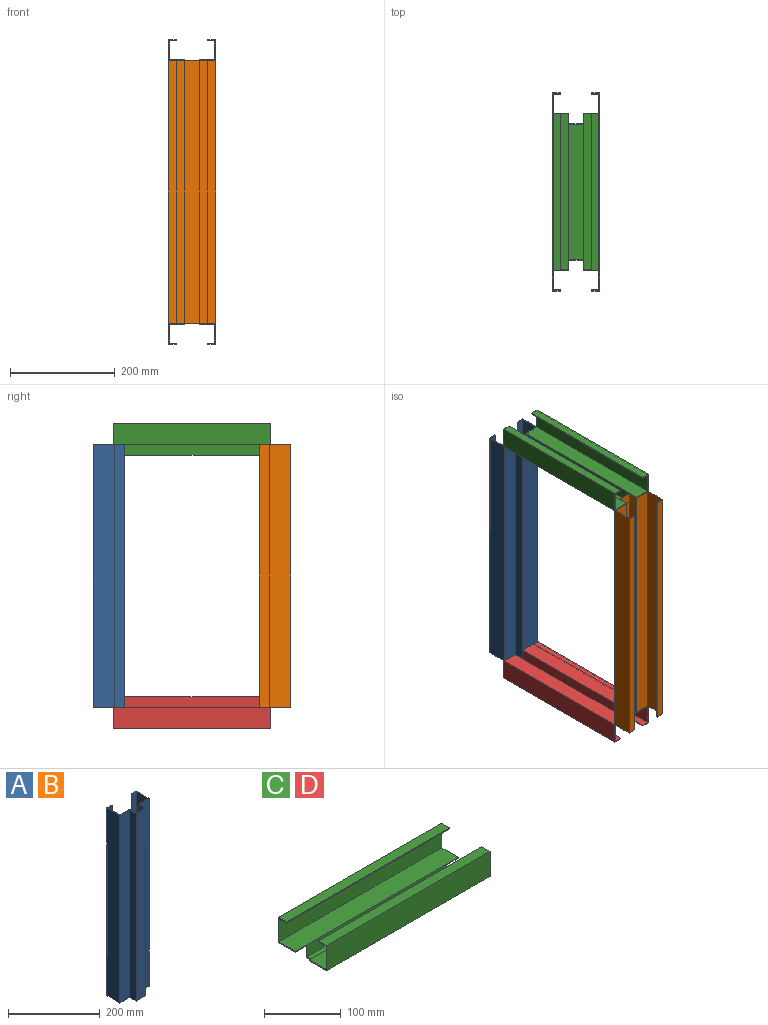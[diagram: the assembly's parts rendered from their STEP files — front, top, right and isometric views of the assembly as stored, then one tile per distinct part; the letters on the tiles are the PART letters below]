
ASSEMBLY  parts=4 mates=12
PART A: 22 faces, bbox 90x60x500 mm
  f0: plane 500x20mm, normal (-1,0,0), area 10000mm2, adj f1,f19,f20,f21
  f1: plane 500x30mm, normal (0,-1,0), area 15000mm2, adj f0,f2,f20,f21
  f2: plane 500x20mm, normal (1,0,0), area 10000mm2, adj f1,f3,f20,f21
  f3: plane 500x30mm, normal (0,-1,0), area 15000mm2, adj f2,f4,f20,f21
  f4: plane 500x40mm, normal (1,0,0), area 20000mm2, adj f3,f5,f20,f21
  f5: plane 500x15mm, normal (0,1,0), area 7500mm2, adj f4,f6,f20,f21
  f6: plane 500x1.6mm, normal (-1,0,0), area 800mm2, adj f5,f7,f20,f21
  f7: plane 500x13.4mm, normal (0,-1,0), area 6700mm2, adj f6,f8,f20,f21
  f8: plane 500x36.8mm, normal (-1,0,0), area 18400mm2, adj f7,f9,f20,f21
  f9: plane 500x30mm, normal (0,1,0), area 15000mm2, adj f8,f10,f20,f21
  f10: plane 500x20mm, normal (-1,0,0), area 10000mm2, adj f9,f11,f20,f21
  f11: plane 500x26.8mm, normal (0,1,0), area 13400mm2, adj f10,f12,f20,f21
  f12: plane 500x20mm, normal (1,0,0), area 10000mm2, adj f11,f13,f20,f21
  f13: plane 500x30mm, normal (0,1,0), area 15000mm2, adj f12,f14,f20,f21
  f14: plane 500x36.8mm, normal (1,0,0), area 18400mm2, adj f13,f15,f20,f21
  f15: plane 500x13.4mm, normal (0,-1,0), area 6700mm2, adj f14,f16,f20,f21
  f16: plane 500x1.6mm, normal (1,0,0), area 800mm2, adj f15,f17,f20,f21
  f17: plane 500x15mm, normal (0,1,0), area 7500mm2, adj f16,f18,f20,f21
  f18: plane 500x40mm, normal (-1,0,0), area 20000mm2, adj f17,f19,f20,f21
  f19: plane 500x30mm, normal (0,-1,0), area 15000mm2, adj f0,f18,f20,f21
  f20: plane 90x60mm, normal (0,0,1), area 373.8mm2, adj f0,f1,f2,f3,f4,f5,f6,f7
  f21: plane 90x60mm, normal (0,0,-1), area 373.8mm2, adj f0,f1,f2,f3,f4,f5,f6,f7
PART B: same geometry as A
PART C: 26 faces, bbox 300x90x60 mm
  f0: plane 256.8x20mm, normal (0,-1,0), area 5136mm2, adj f1,f23,f24,f25
  f1: plane 256.8x30mm, normal (0,0,-1), area 7704mm2, adj f0,f2,f24,f25
  f2: plane 256.8x20mm, normal (0,1,0), area 5136mm2, adj f1,f8,f24,f25
  f3: plane 256.8x26.8mm, normal (0,0,1), area 6882.2mm2, adj f15,f16,f24,f25
  f4: plane 40x31.6mm, normal (1,0,0), area 133.4mm2, adj f16,f17,f18,f19,f20,f21,f22,f23
  f5: plane 40x31.6mm, normal (1,0,0), area 133.4mm2, adj f8,f9,f10,f11,f12,f13,f14,f15
  f6: plane 40x31.6mm, normal (-1,0,0), area 133.4mm2, adj f16,f17,f18,f19,f20,f21,f22,f23
  f7: plane 40x31.6mm, normal (-1,0,0), area 133.4mm2, adj f8,f9,f10,f11,f12,f13,f14,f15
  f8: plane 300x31.6mm, normal (0,0,-1), area 9069.1mm2, adj f2,f5,f7,f9,f15,f24,f25
  f9: plane 300x40mm, normal (0,1,0), area 12000mm2, adj f5,f7,f8,f10
  f10: plane 300x15mm, normal (0,0,1), area 4500mm2, adj f5,f7,f9,f11
  f11: plane 300x1.6mm, normal (0,-1,0), area 480mm2, adj f5,f7,f10,f12
  f12: plane 300x13.4mm, normal (0,0,-1), area 4020mm2, adj f5,f7,f11,f13
  f13: plane 300x36.8mm, normal (0,-1,0), area 11040mm2, adj f5,f7,f12,f14
  f14: plane 300x30mm, normal (0,0,1), area 9000mm2, adj f5,f7,f13,f15
  f15: plane 300x20mm, normal (0,-1,0), area 5205.1mm2, adj f3,f5,f7,f8,f14,f24,f25
  f16: plane 300x20mm, normal (0,1,0), area 5205.1mm2, adj f3,f4,f6,f17,f23,f24,f25
  f17: plane 300x30mm, normal (0,0,1), area 9000mm2, adj f4,f6,f16,f18
  f18: plane 300x36.8mm, normal (0,1,0), area 11040mm2, adj f4,f6,f17,f19
  f19: plane 300x13.4mm, normal (0,0,-1), area 4020mm2, adj f4,f6,f18,f20
  f20: plane 300x1.6mm, normal (0,1,0), area 480mm2, adj f4,f6,f19,f21
  f21: plane 300x15mm, normal (0,0,1), area 4500mm2, adj f4,f6,f20,f22
  f22: plane 300x40mm, normal (0,-1,0), area 12000mm2, adj f4,f6,f21,f23
  f23: plane 300x31.6mm, normal (0,0,-1), area 9069.1mm2, adj f0,f4,f6,f16,f22,f24,f25
  f24: plane 30x20mm, normal (1,0,0), area 106.9mm2, adj f0,f1,f2,f3,f8,f15,f16,f23
  f25: plane 30x20mm, normal (-1,0,0), area 106.9mm2, adj f0,f1,f2,f3,f8,f15,f16,f23
PART D: same geometry as C
PLACE A rot(axis=(0.08,-0.12,0.99),0deg) t=(2.66,156.17,-399.75)mm fixed
PLACE B rot(axis=(0,0,1),180deg) t=(2.66,-180.63,-399.75)mm
PLACE C rot(axis=(0,0,-1),90deg) t=(2.36,137.77,112.95)mm
PLACE D rot(axis=(0.71,-0.71,0),180deg) t=(2.96,137.77,-412.45)mm
MATE planar C.f8 <-> A.f20  axis (0,0,-1) through (32.54,-12.23,100.25)mm
MATE parallel D.f1 <-> C.f1  axis (0,0,1) through (-12.34,-12.23,-379.75)mm
MATE planar B.f12 <-> C.f15  axis (-1,0,0) through (16.06,-152.23,-149.75)mm
MATE planar D.f25 <-> A.f1  axis (0,1,0) through (2.66,116.17,-386.06)mm
MATE planar D.f23 <-> A.f21  axis (0,0,1) through (32.54,-12.23,-399.75)mm
MATE planar C.f2 <-> A.f2  axis (1,0,0) through (17.66,-12.23,90.25)mm
MATE planar A.f4 <-> D.f22  axis (1,0,0) through (47.66,156.17,-149.75)mm
MATE planar A.f1 <-> C.f25  axis (0,-1,0) through (2.66,116.17,-149.75)mm
MATE parallel D.f25 <-> C.f7  axis (0,1,0) through (2.66,116.17,-386.06)mm
MATE planar B.f1 <-> C.f24  axis (0,1,0) through (2.66,-140.63,-149.75)mm
MATE planar C.f24 <-> B.f1  axis (0,-1,0) through (2.66,-140.63,86.56)mm
MATE planar B.f20 <-> C.f8  axis (0,0,1) through (2.66,-168.27,100.25)mm
